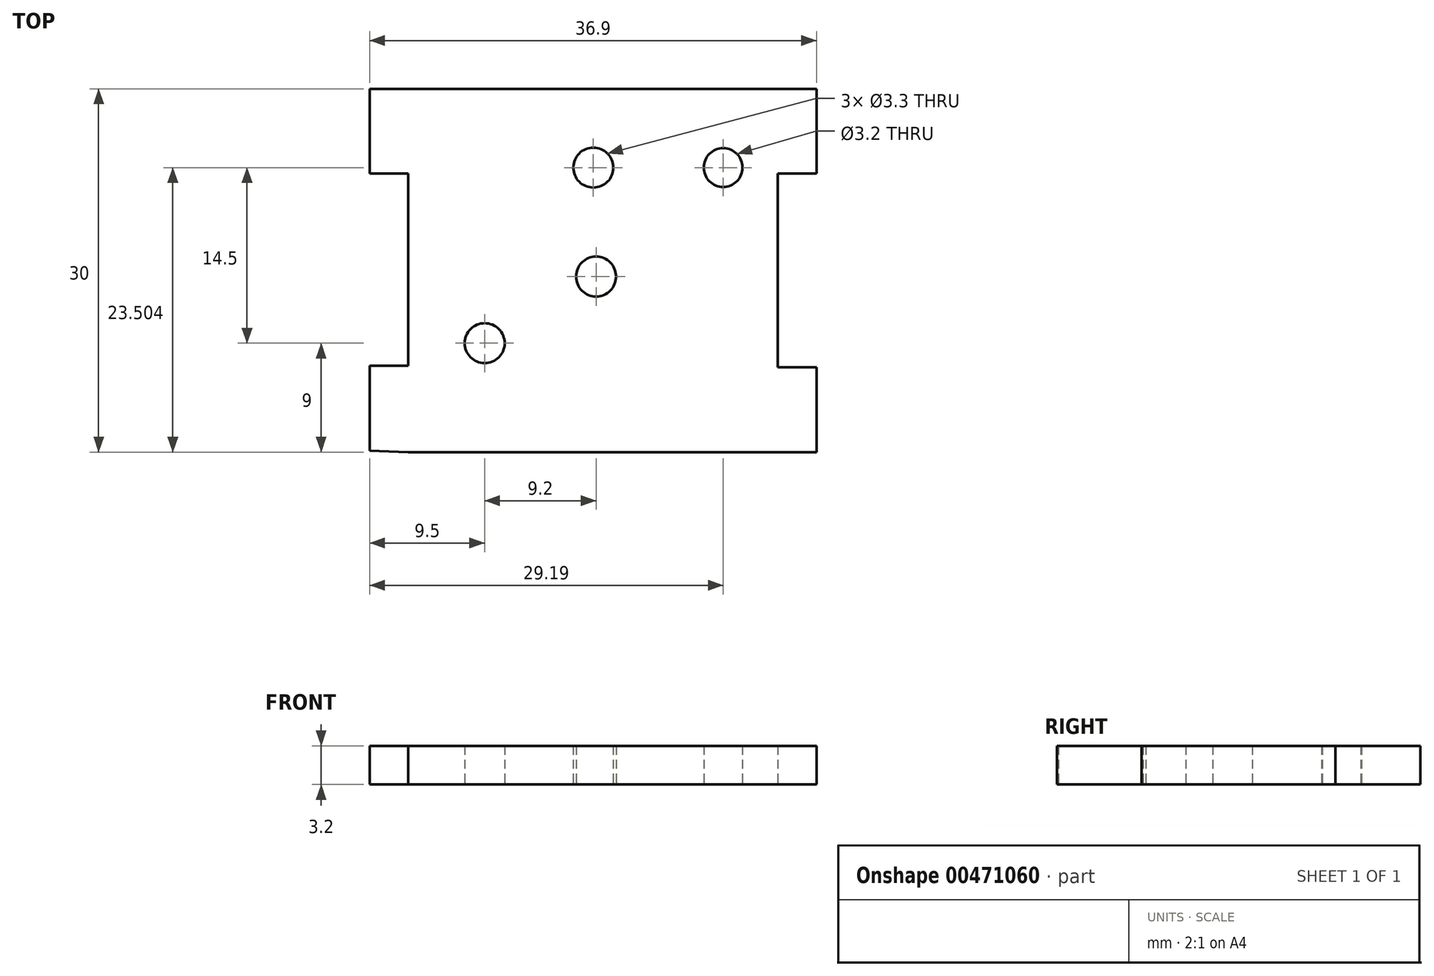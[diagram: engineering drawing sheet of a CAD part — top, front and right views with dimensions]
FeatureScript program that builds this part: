
annotation { "Feature Type Name" : "Feature", "Feature Type Description" : "" }
export const myFeature = defineFeature(function(context is Context, id is Id, definition is map)
    precondition{}
    {
        {
            var Q0;
            Q0=qCreatedBy(makeId("Top.planeOp"),FACE);
            var sketch = newSketch(context, id + "F0", { "sketchPlane" : qUnion([Q0])});
            skLineSegment(sketch, "E0.bottom", {"start": v(-50.01, 4.53) * mm, "end": v(-19.51, 4.53) * mm});
            skLineSegment(sketch, "E0.top", {"start": v(-50.01, -25.47) * mm, "end": v(-19.51, -25.47) * mm});
            skLineSegment(sketch, "E0.left", {"start": v(-50.01, -2.47) * mm, "end": v(-50.01, -18.34) * mm});
            skLineSegment(sketch, "E0.right", {"start": v(-19.51, -2.47) * mm, "end": v(-19.51, -18.47) * mm});
            skCircle(sketch, "E1", {"center": v(-34.74, -1.97) * mm, "radius": 1.65 * mm});
            skCircle(sketch, "E2", {"center": v(-34.51, -10.97) * mm, "radius": 1.65 * mm});
            skLineSegment(sketch, "E3", {"start": v(-50.01, -18.34) * mm, "end": v(-53.21, -18.34) * mm});
            skLineSegment(sketch, "E4", {"start": v(-53.21, -18.34) * mm, "end": v(-53.21, -25.34) * mm});
            skLineSegment(sketch, "E5", {"start": v(-53.21, -25.34) * mm, "end": v(-50.01, -25.47) * mm});
            skLineSegment(sketch, "E6", {"start": v(-19.51, -25.47) * mm, "end": v(-16.31, -25.47) * mm});
            skLineSegment(sketch, "E7", {"start": v(-16.31, -25.47) * mm, "end": v(-16.31, -18.47) * mm});
            skLineSegment(sketch, "E8", {"start": v(-16.31, -18.47) * mm, "end": v(-19.51, -18.47) * mm});
            skLineSegment(sketch, "E9", {"start": v(-19.51, 4.53) * mm, "end": v(-16.31, 4.53) * mm});
            skLineSegment(sketch, "E10", {"start": v(-16.31, 4.53) * mm, "end": v(-16.31, -2.47) * mm});
            skLineSegment(sketch, "E11", {"start": v(-16.31, -2.47) * mm, "end": v(-19.51, -2.47) * mm});
            skLineSegment(sketch, "E12", {"start": v(-50.01, 4.53) * mm, "end": v(-53.21, 4.53) * mm});
            skLineSegment(sketch, "E13", {"start": v(-53.21, 4.53) * mm, "end": v(-53.21, -2.47) * mm});
            skLineSegment(sketch, "E14", {"start": v(-53.21, -2.47) * mm, "end": v(-50.01, -2.47) * mm});
            skCircle(sketch, "E15", {"center": v(-43.71, -16.47) * mm, "radius": 1.65 * mm});
            skCircle(sketch, "E16", {"center": v(-24.02, -1.97) * mm, "radius": 1.6 * mm});
            skSolve(sketch);
        }
        {
            var Q0;
            Q0 = qSketchRegion(id + "F0", true);
            extrude(context, id + "F1", {"entities" : qUnion([Q0]), "depth" : 3.2 * mm, "offsetDistance" : 25 * mm});
        }
    });
